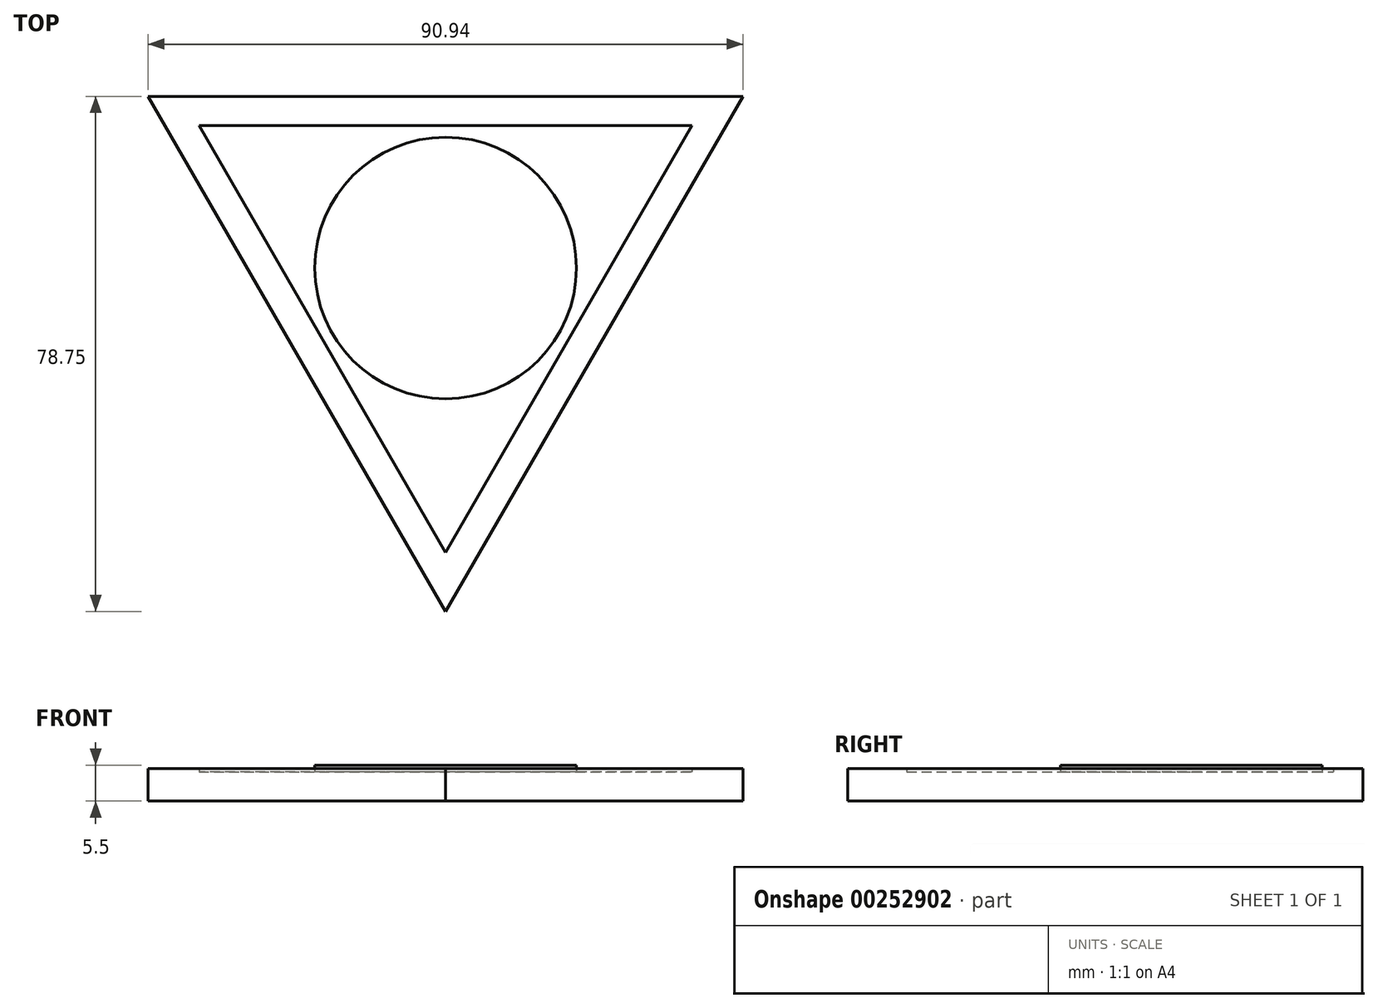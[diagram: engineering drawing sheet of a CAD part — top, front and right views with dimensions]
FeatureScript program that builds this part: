
annotation { "Feature Type Name" : "Feature", "Feature Type Description" : "" }
export const myFeature = defineFeature(function(context is Context, id is Id, definition is map)
    precondition{}
    {
        {
            var Q0;
            Q0=qCreatedBy(makeId("Top.planeOp"),FACE);
            var sketch = newSketch(context, id + "F0", { "sketchPlane" : qUnion([Q0])});
            skCircle(sketch, "E0", {"center": v(0, 0) * mm, "radius": 20.5 * mm});
            skSolve(sketch);
        }
        {
            var Q0;
            Q0=qCreatedBy(makeId("Top.planeOp"),FACE);
            var sketch = newSketch(context, id + "F1", { "sketchPlane" : qUnion([Q0])});
            skCircle(sketch, "E1.cCircle", {"center": v(0, 0) * mm, "radius": 26.25 * mm, "construction": true});
            skLineSegment(sketch, "E1.0", {"start": v(-45.47, 26.25) * mm, "end": v(45.47, 26.25) * mm});
            skLineSegment(sketch, "E1.1", {"start": v(45.47, 26.25) * mm, "end": v(0, -52.5) * mm});
            skLineSegment(sketch, "E1.2", {"start": v(0, -52.5) * mm, "end": v(-45.47, 26.25) * mm});
            skPoint(sketch, "E1.0.midPoint", {"position": v(0, 26.25) * mm});
            skSolve(sketch);
        }
        {
            var Q0;
            Q0=makeQuery(id+"F1.imprint","IMPRINT",FACE,{"disambiguationData":[TD([[makeQuery(id+"F1.imprint","IMPRINT",EDGE,{"derivedFrom":sQuery(id+"F1.wireOp",EDGE,"E1.0")}),-1.0]])]});
            extrude(context, id + "F2", {"entities" : qUnion([Q0]), "depth" : 5 * mm});
        }
        {
            var Q0;
            Q0=makeQuery(id+"F0.imprint","IMPRINT",FACE,{"disambiguationData":[TD([[makeQuery(id+"F0.imprint","IMPRINT",EDGE,{"derivedFrom":sQuery(id+"F0.wireOp",EDGE,"E0")}),1.0]])]});
            extrude(context, id + "F3", {"entities" : qUnion([Q0]), "operationType" : NewBodyOperationType.ADD, "depth" : 5 * mm});
        }
        {
            var Q0;
            Q0=makeQuery(id+"F2.opExtrude","CAP_FACE",FACE,{"disambiguationData":[OSD([sQuery(id+"F1.wireOp",EDGE,"E1.0"),sQuery(id+"F1.wireOp",EDGE,"E1.1"),sQuery(id+"F1.wireOp",EDGE,"E1.2")])],"isStart":false});
            shell(context, id + "F4", {"entities" : qUnion([Q0]), "thickness" : 4.5 * mm});
        }
        {
            var Q0;
            Q0=makeQuery(id+"F4.opShell","OFFSET_FACE",FACE,{"disambiguationData":[OSD([sQuery(id+"F1.wireOp",EDGE,"E1.0"),sQuery(id+"F1.wireOp",EDGE,"E1.1"),sQuery(id+"F1.wireOp",EDGE,"E1.2")])]});
            var sketch = newSketch(context, id + "F5", { "sketchPlane" : qUnion([Q0])});
            skCircle(sketch, "E2", {"center": v(0, 0) * mm, "radius": 20 * mm});
            skSolve(sketch);
        }
        {
            var Q0;
            Q0=makeQuery(id+"F5.imprint","IMPRINT",FACE,{"disambiguationData":[TD([[makeQuery(id+"F5.imprint","IMPRINT",EDGE,{"derivedFrom":sQuery(id+"F5.wireOp",EDGE,"E2")}),1.0]])]});
            extrude(context, id + "F6", {"entities" : qUnion([Q0]), "operationType" : NewBodyOperationType.ADD, "depth" : 1 * mm});
        }
    });
